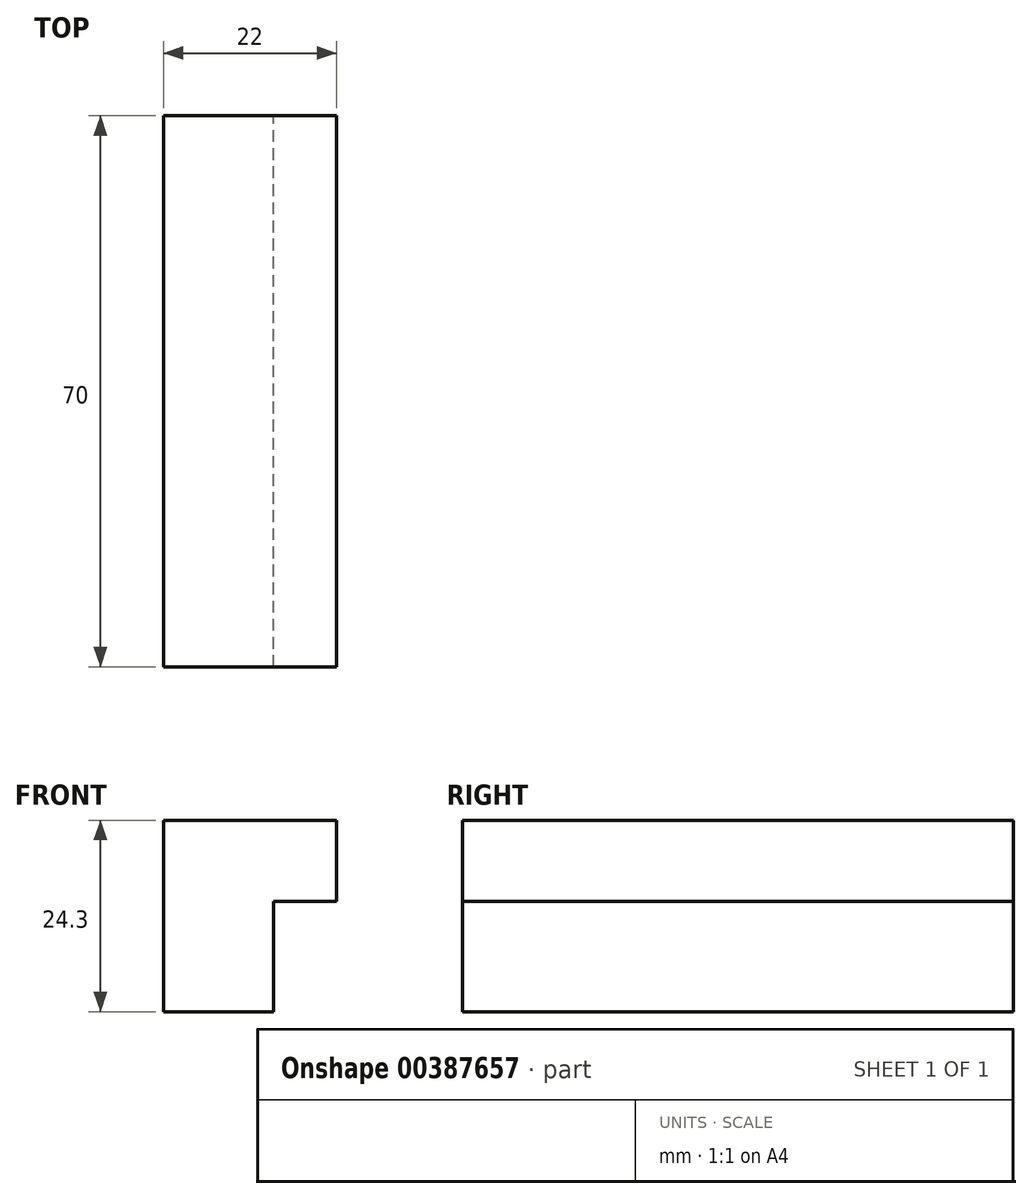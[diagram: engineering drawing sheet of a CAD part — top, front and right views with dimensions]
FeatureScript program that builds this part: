
annotation { "Feature Type Name" : "Feature", "Feature Type Description" : "" }
export const myFeature = defineFeature(function(context is Context, id is Id, definition is map)
    precondition{}
    {
        {
            var Q0;
            Q0=qCreatedBy(makeId("Front.planeOp"),FACE);
            var sketch = newSketch(context, id + "F0", { "sketchPlane" : qUnion([Q0])});
            skLineSegment(sketch, "E0.bottom", {"start": v(-6.55, 0) * mm, "end": v(7.45, 0) * mm});
            skLineSegment(sketch, "E0.left", {"start": v(-6.55, 0) * mm, "end": v(-6.55, 14) * mm});
            skLineSegment(sketch, "E0.right", {"start": v(7.45, 0) * mm, "end": v(7.45, 14) * mm});
            skPoint(sketch, "E1", {"position": v(-6.55, 24.3) * mm});
            skPoint(sketch, "E2", {"position": v(7.45, 24.3) * mm});
            skPoint(sketch, "E3", {"position": v(15.45, 24.3) * mm});
            skPoint(sketch, "E4", {"position": v(15.45, 14) * mm});
            skLineSegment(sketch, "E5", {"start": v(-6.55, 14) * mm, "end": v(-6.55, 24.3) * mm});
            skLineSegment(sketch, "E6", {"start": v(-6.55, 24.3) * mm, "end": v(15.45, 24.3) * mm});
            skLineSegment(sketch, "E7", {"start": v(7.45, 14) * mm, "end": v(15.45, 14) * mm});
            skLineSegment(sketch, "E8", {"start": v(15.45, 14) * mm, "end": v(15.45, 24.3) * mm});
            skSolve(sketch);
        }
        {
            var Q0;
            Q0=makeQuery(id+"F0.imprint","IMPRINT",FACE,{"disambiguationData":[TD([[makeQuery(id+"F0.imprint","IMPRINT",EDGE,{"derivedFrom":sQuery(id+"F0.wireOp",EDGE,"E0.bottom")}),1.0]])]});
            extrude(context, id + "F1", {"entities" : qUnion([Q0]), "depth" : 70 * mm});
        }
    });
